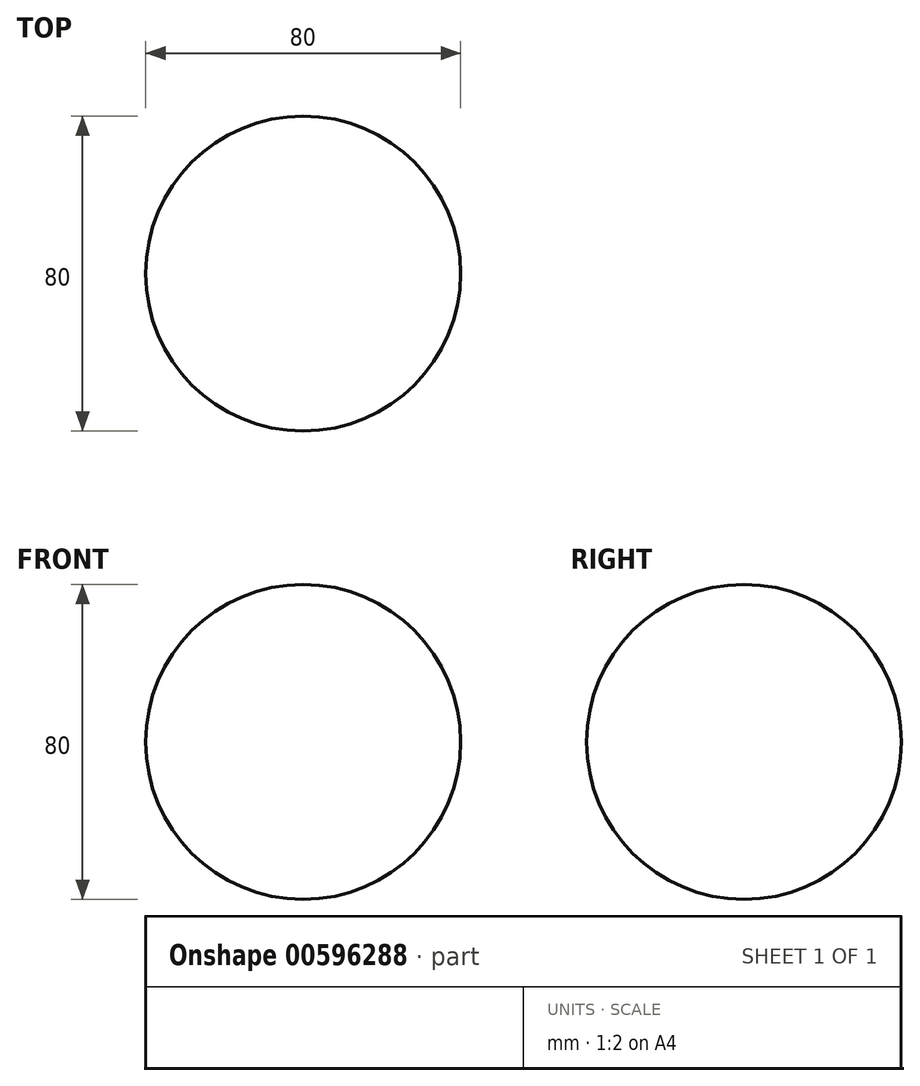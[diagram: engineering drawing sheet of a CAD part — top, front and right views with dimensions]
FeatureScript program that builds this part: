
annotation { "Feature Type Name" : "Feature", "Feature Type Description" : "" }
export const myFeature = defineFeature(function(context is Context, id is Id, definition is map)
    precondition{}
    {
        {
            var Q0;
            Q0=qCreatedBy(makeId("Front.planeOp"),FACE);
            var sketch = newSketch(context, id + "F0", { "sketchPlane" : qUnion([Q0])});
            skArc(sketch, "E0", {"start": v(0, -40) * mm, "mid": v(40, 0) * mm, "end": v(0, 40) * mm});
            skLineSegment(sketch, "E1", {"start": v(0, 40) * mm, "end": v(0, -40) * mm});
            skSolve(sketch);
        }
        {
            var Q0;
            Q0 = qSketchRegion(id + "F0", true);
            var Q1;
            Q1=sQuery(id+"F0.wireOp",EDGE,"E1");
            revolve(context, id + "F1", {"entities" : qUnion([Q0]), "axis" : qUnion([Q1]), "revolveType" : RevolveType.FULL});
        }
    });
